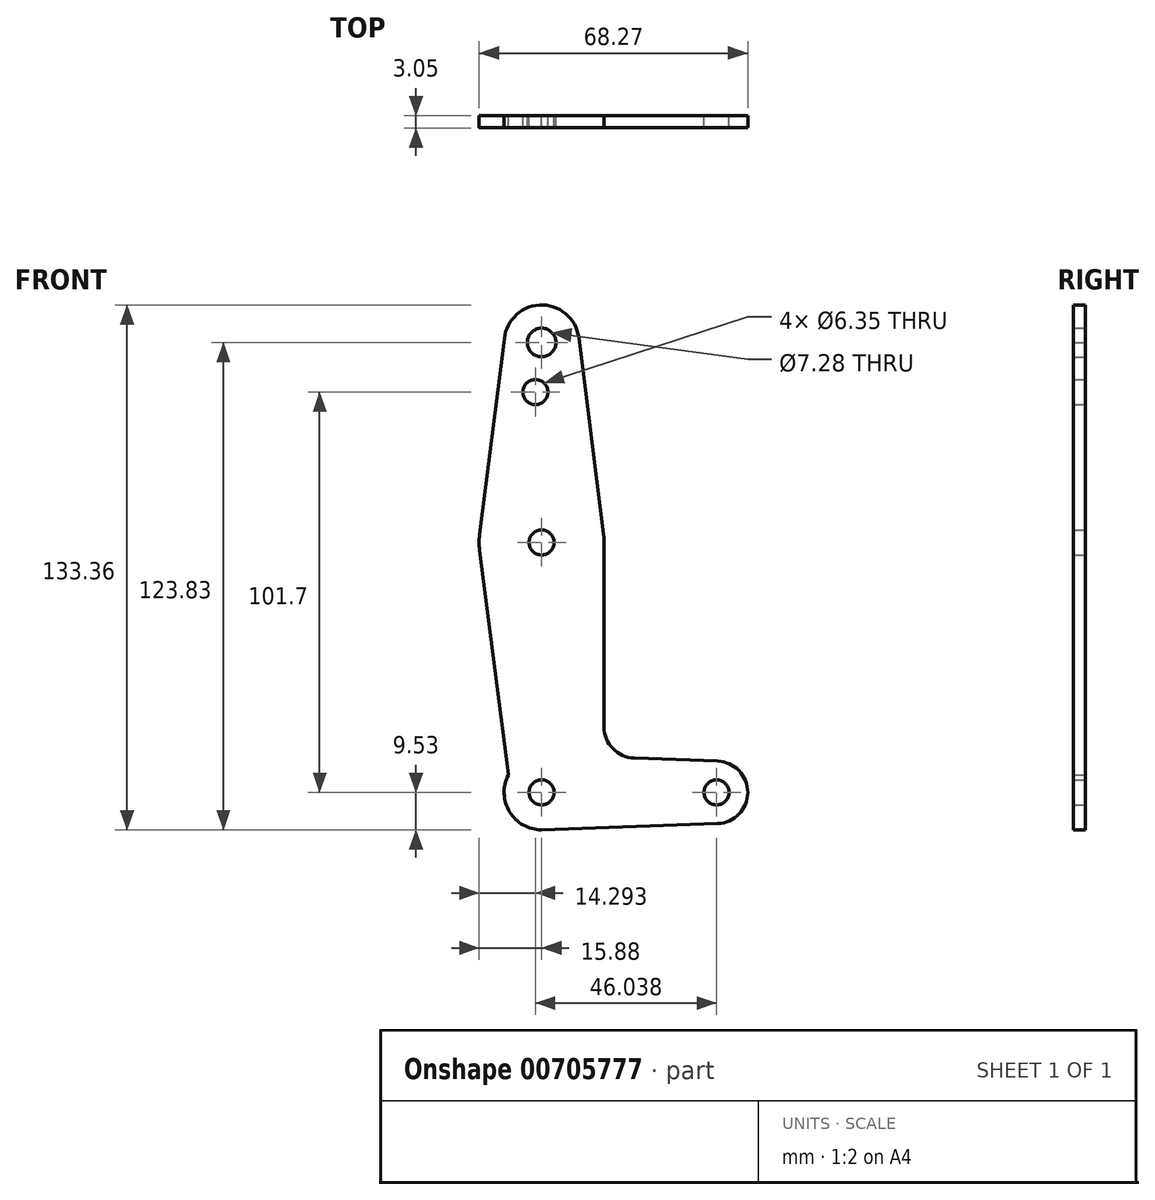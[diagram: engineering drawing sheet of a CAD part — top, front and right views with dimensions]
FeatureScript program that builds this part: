
annotation { "Feature Type Name" : "Feature", "Feature Type Description" : "" }
export const myFeature = defineFeature(function(context is Context, id is Id, definition is map)
    precondition{}
    {
        {
            var Q0;
            Q0=qCreatedBy(makeId("Front.planeOp"),FACE);
            var sketch = newSketch(context, id + "F0", { "sketchPlane" : qUnion([Q0])});
            skLineSegment(sketch, "E0", {"start": v(0, 0) * mm, "end": v(44.45, 0) * mm, "construction": true});
            skLineSegment(sketch, "E1", {"start": v(0, 0) * mm, "end": v(0, 114.3) * mm, "construction": true});
            skLineSegment(sketch, "E2", {"start": v(0, 0) * mm, "end": v(0, 63.5) * mm, "construction": true});
            skCircle(sketch, "E3", {"center": v(0, 114.3) * mm, "radius": 9.53 * mm});
            skCircle(sketch, "E4", {"center": v(0, 63.5) * mm, "radius": 15.88 * mm});
            skCircle(sketch, "E5", {"center": v(0, 0) * mm, "radius": 9.53 * mm});
            skCircle(sketch, "E6", {"center": v(44.45, 0) * mm, "radius": 7.94 * mm});
            skLineSegment(sketch, "E7", {"start": v(0, -9.53) * mm, "end": v(44.73, -7.93) * mm});
            skLineSegment(sketch, "E8", {"start": v(9.45, 115.5) * mm, "end": v(15.75, 65.48) * mm});
            skLineSegment(sketch, "E9", {"start": v(23.54, 8.69) * mm, "end": v(44.73, 7.93) * mm});
            skLineSegment(sketch, "E10", {"start": v(15.87, 63.5) * mm, "end": v(15.88, 16.63) * mm});
            skLineSegment(sketch, "E11", {"start": v(-9.53, 114.3) * mm, "end": v(-15.75, 65.5) * mm});
            skLineSegment(sketch, "E12", {"start": v(-15.75, 61.5) * mm, "end": v(-7.9, 0) * mm});
            skArc(sketch, "E13.filletArc", {"start": v(15.88, 16.63) * mm, "mid": v(18.1, 11.11) * mm, "end": v(23.54, 8.69) * mm});
            skCircle(sketch, "E14", {"center": v(0, 114.3) * mm, "radius": 3.64 * mm});
            skCircle(sketch, "E15", {"center": v(0, 63.5) * mm, "radius": 3.18 * mm});
            skCircle(sketch, "E16", {"center": v(0, 0) * mm, "radius": 3.18 * mm});
            skCircle(sketch, "E17", {"center": v(44.45, 0) * mm, "radius": 3.18 * mm});
            skCircle(sketch, "E18", {"center": v(-1.59, 101.7) * mm, "radius": 3.18 * mm});
            skSolve(sketch);
        }
        {
            var Q0;
            {var subQ0=sQuery(id+"F0.wireOp",EDGE,"E8");Q0=makeQuery(id+"F0.imprint","IMPRINT",FACE,{"disambiguationData":[TD([[makeQuery(id+"F0.imprint","IMPRINT",EDGE,{"derivedFrom":subQ0}),-1.0]])]});}
            var Q1;
            Q1=makeQuery(id+"F0.imprint","IMPRINT",FACE,{"disambiguationData":[TD([[makeQuery(id+"F0.imprint","IMPRINT",EDGE,{"derivedFrom":sQuery(id+"F0.wireOp",EDGE,"E14")}),-1.0]])]});
            var Q2;
            Q2=makeQuery(id+"F0.imprint","IMPRINT",FACE,{"disambiguationData":[TD([[makeQuery(id+"F0.imprint","IMPRINT",EDGE,{"derivedFrom":sQuery(id+"F0.wireOp",EDGE,"E15")}),-1.0]])]});
            var Q3;
            {var subQ5=sQuery(id+"F0.wireOp",EDGE,"E9");Q3=makeQuery(id+"F0.imprint","IMPRINT",FACE,{"disambiguationData":[TD([[makeQuery(id+"F0.imprint","IMPRINT",EDGE,{"derivedFrom":subQ5}),-1.0]])]});}
            var Q4;
            Q4=makeQuery(id+"F0.imprint","IMPRINT",FACE,{"disambiguationData":[TD([[makeQuery(id+"F0.imprint","IMPRINT",EDGE,{"derivedFrom":sQuery(id+"F0.wireOp",EDGE,"E16")}),-1.0]])]});
            var Q5;
            Q5=makeQuery(id+"F0.imprint","IMPRINT",FACE,{"disambiguationData":[TD([[makeQuery(id+"F0.imprint","IMPRINT",EDGE,{"derivedFrom":sQuery(id+"F0.wireOp",EDGE,"E17")}),-1.0]])]});
            extrude(context, id + "F1", {"entities" : qUnion([Q0, Q1, Q2, Q3, Q4, Q5]), "depth" : 3.05 * mm, "offsetDistance" : 25.4 * mm});
        }
    });
